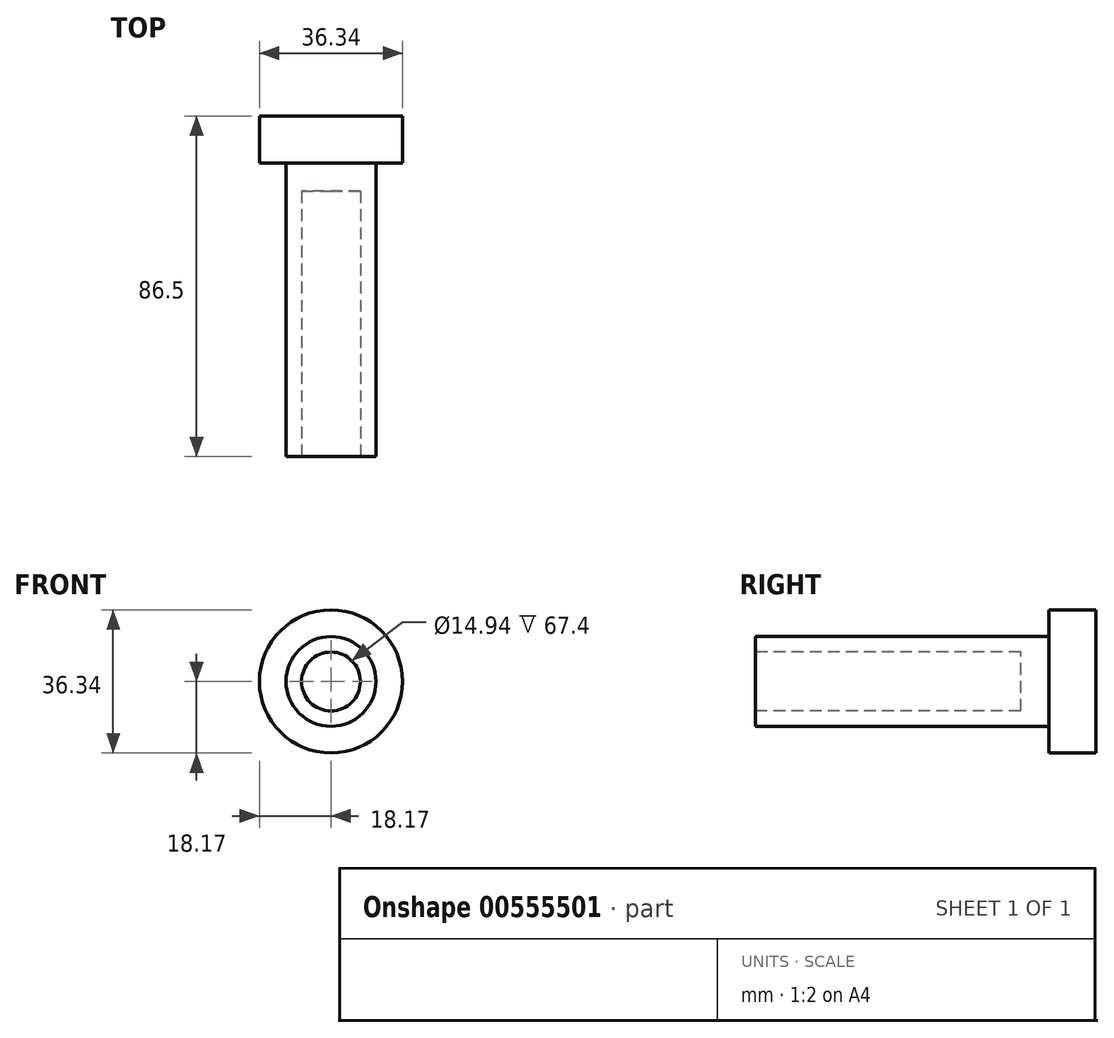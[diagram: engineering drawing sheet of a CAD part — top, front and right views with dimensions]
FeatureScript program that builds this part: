
annotation { "Feature Type Name" : "Feature", "Feature Type Description" : "" }
export const myFeature = defineFeature(function(context is Context, id is Id, definition is map)
    precondition{}
    {
        {
            var Q0;
            Q0=qCreatedBy(makeId("Front.planeOp"),FACE);
            var sketch = newSketch(context, id + "F0", { "sketchPlane" : qUnion([Q0])});
            skCircle(sketch, "E0", {"center": v(1.43, 0) * mm, "radius": 11.4 * mm});
            skSolve(sketch);
        }
        {
            var Q0;
            Q0 = qSketchRegion(id + "F0", true);
            extrude(context, id + "F1", {"entities" : qUnion([Q0]), "depth" : 74.6 * mm, "offsetDistance" : 25 * mm});
        }
        {
            var Q0;
            Q0=makeQuery(id+"F1.opExtrude","CAP_FACE",FACE,{"disambiguationData":[OSD([sQuery(id+"F0.wireOp",EDGE,"E0")])],"isStart":true});
            var sketch = newSketch(context, id + "F2", { "sketchPlane" : qUnion([Q0])});
            skCircle(sketch, "E1", {"center": v(-1.43, 0) * mm, "radius": 18.17 * mm});
            skSolve(sketch);
        }
        {
            var Q0;
            Q0 = qSketchRegion(id + "F2", true);
            extrude(context, id + "F3", {"entities" : qUnion([Q0]), "operationType" : NewBodyOperationType.ADD, "depth" : 11.9 * mm, "offsetDistance" : 25 * mm});
        }
        {
            var Q0;
            Q0=makeQuery(id+"F1.opExtrude","CAP_FACE",FACE,{"disambiguationData":[OSD([sQuery(id+"F0.wireOp",EDGE,"E0")])],"isStart":false});
            var sketch = newSketch(context, id + "F4", { "sketchPlane" : qUnion([Q0])});
            skCircle(sketch, "E2", {"center": v(1.43, 0) * mm, "radius": 7.47 * mm});
            skSolve(sketch);
        }
        {
            var Q0;
            Q0 = qSketchRegion(id + "F4", true);
            extrude(context, id + "F5", {"entities" : qUnion([Q0]), "operationType" : NewBodyOperationType.REMOVE, "oppositeDirection" : true, "depth" : 67.4 * mm, "offsetDistance" : 25 * mm});
        }
    });
